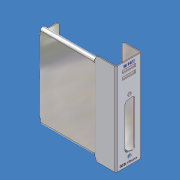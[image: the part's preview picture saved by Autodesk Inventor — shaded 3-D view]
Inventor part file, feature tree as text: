
AUTODESK INVENTOR PART (.ipt)
format: ipt  version: unknown  size: 581,632 bytes
history: native  units: mm (DEFAULTED — no unit token found)
features: sketch x12, sheet_metal_op x11, other x9, chamfer x3, extrude x1, pattern_linear x1
ambient origin geometry x8: Origin, YZ Plane, XZ Plane, XY Plane, X Axis, Y Axis, Z Axis, Center Point
feature tree (37):
  sheet_metal_op  "Face1"
  sheet_metal_op  "Flange1"
  sheet_metal_op  "Flange2"
  chamfer  "Corner Round1"
  sheet_metal_op  "Face2"
  sheet_metal_op  "Flange3"
  chamfer  "Corner Round2"
  sheet_metal_op  "Hem2"
  sheet_metal_op  "Hem3"
  chamfer  "Corner Round3"
  extrude  "Extrusion1"  Depth=80.5688mm
  pattern_linear  "Rectangular Pattern1"  Spacing1=1.778mm  [1 undecoded]
  sketch  "Sketch1"  dims[d0=22.86mm d1=80.5688mm]
  other  "Plate1"
  sketch  "Sketch2"  dims[d2=0.7874mm]
  other  "Plate2"
  sheet_metal_op  "Bend1"
  sketch  "Sketch3"  dims[d3=0.7874mm]
  other  "Plate3"
  sheet_metal_op  "Bend2"
  sketch  "Sketch4"  dims[d4=0.3937mm]
  other  "Plate4"
  sheet_metal_op  "Bend3"
  sketch  "Sketch5"  dims[d5=1.5748mm]
  other  "Plate5"
  sheet_metal_op  "Bend4"
  sketch  "Sketch8"  dims[d6=0.7874mm]
  sketch  "Sketch9"  dims[d7=16.51mm d8=90.0deg d9=0.7874mm]
  sketch  "Sketch10"  dims[d10=0.7874mm]
  sketch  "Sketch11"  dims[d11=0.3937mm]
  sketch  "Sketch12"  dims[d12=1.5748mm]
  sketch  "Sketch15"  dims[d13=0.7874mm]
  other  "Image4"
  sketch  "Sketch16"  dims[d14=17.526mm d15=90.0deg d16=0.7874mm d17=1.778mm d18=0.7874mm d19=0.7874mm d20=0.3937mm d21=1.5748mm d22=0.7874mm d23=73.66mm d24=50.8mm d25=5.08mm d26=5.08mm d27=0.7874mm d28=0.3937mm d29=1.5748mm d30=0.7874mm d31=17.78mm d32=90.0deg d33=0.7874mm d42=1.778mm d43=0.7874mm d44=0.0mm d45=0.7874mm d46=0.3937mm d47=1.5748mm d48=0.7874mm d49=3.1496mm d50=2.7432mm d51=1.3716mm d52=0.7874mm d53=0.3937mm d54=1.5748mm d55=0.7874mm d56=3.1496mm d57=2.7432mm d58=1.3716mm d59=12.7mm d60=20.32mm d62=5.588mm d63=0.7874mm d64=0.0mm d65=1.778mm d66=3.175mm d67=3.048mm d69=23.5204mm d76=30.48mm d78=0.508mm d81=-15.707963mm d94=2.54mm d95=11.43mm d96=4.064mm d97=5.588mm d98=2.54mm d99=0.0mm d100=20.0mm d102=5.0mm]
  other  "Cut1"
  other  "Cut2"
  other  "iFeature14:1"
note: 1 required parameter value undecoded (feature->parameter linkage not recoverable at this tier; creation-order binding heuristic only, values carry confidence <= 0.55)
